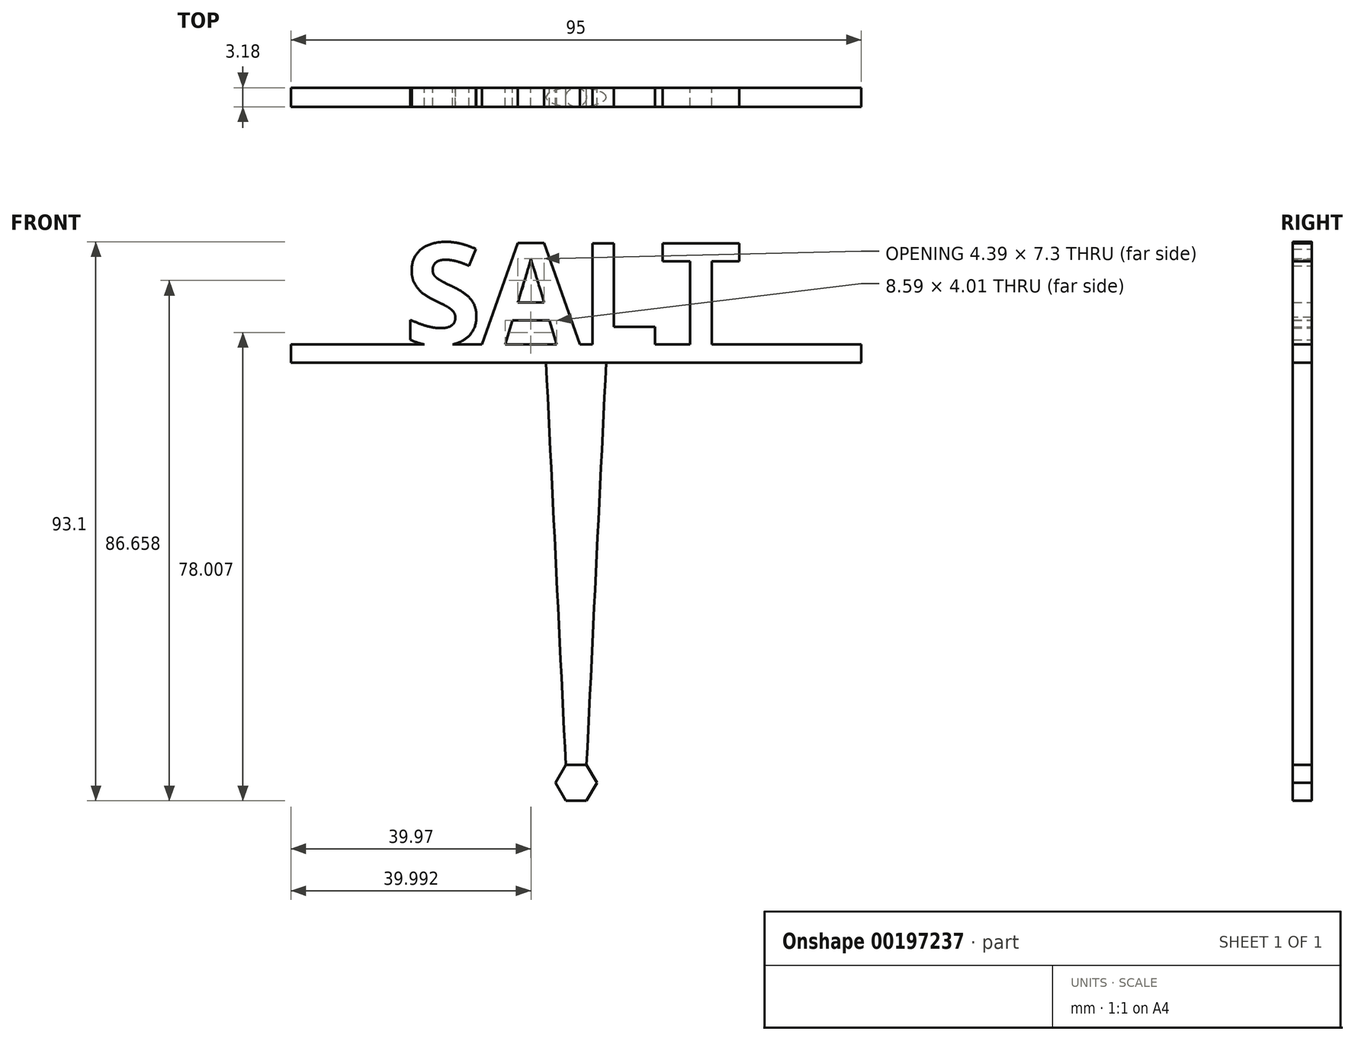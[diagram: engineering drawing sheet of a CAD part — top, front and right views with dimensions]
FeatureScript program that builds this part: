
annotation { "Feature Type Name" : "Feature", "Feature Type Description" : "" }
export const myFeature = defineFeature(function(context is Context, id is Id, definition is map)
    precondition{}
    {
        {
            var Q0;
            Q0=qCreatedBy(makeId("Front.planeOp"),FACE);
            var sketch = newSketch(context, id + "F0", { "sketchPlane" : qUnion([Q0])});
            skLineSegment(sketch, "E0.bottom", {"start": v(-47.5, 3) * mm, "end": v(47.5, 3) * mm});
            skLineSegment(sketch, "E0.top", {"start": v(-47.5, 0) * mm, "end": v(47.5, 0) * mm});
            skLineSegment(sketch, "E0.left", {"start": v(-47.5, 3) * mm, "end": v(-47.5, 0) * mm});
            skLineSegment(sketch, "E0.right", {"start": v(47.5, 3) * mm, "end": v(47.5, 0) * mm});
            skText(sketch, "E1", { "text": "SALT", "fontName": "OpenSans-Bold.ttf"});
            const initialGuessF0  = {"E1": [-0.02868, 0.003, 1, 0, 0.017]};
            skSetInitialGuess(sketch, initialGuessF0);
            skSolve(sketch);
        }
        {
            var Q0;
            Q0=qSketchRegion(id+"F0",true);
            extrude(context, id + "F1", {"entities" : qUnion([Q0]), "depth" : 3.17 * mm});
        }
        {
            var Q0;
            Q0=qCreatedBy(makeId("Top.planeOp"),FACE);
            var sketch = newSketch(context, id + "F2", { "sketchPlane" : qUnion([Q0])});
            skLineSegment(sketch, "E2.bottom", {"start": v(0, 0) * mm, "end": v(2.5, 0) * mm, "construction": true});
            skLineSegment(sketch, "E2.top", {"start": v(0, -3.17) * mm, "end": v(2.5, -3.17) * mm, "construction": true});
            skLineSegment(sketch, "E2.left", {"start": v(0, 0) * mm, "end": v(0, -3.18) * mm, "construction": true});
            skLineSegment(sketch, "E2.right", {"start": v(2.5, 0) * mm, "end": v(2.5, -3.17) * mm, "construction": true});
            skEllipse(sketch, "E3", {"center": v(0, -1.59) * mm, "majorRadius": 5 * mm, "minorRadius": 1.59 * mm, "majorAxis": v(1, 0)});
            skSolve(sketch);
        }
        {
            var Q0;
            Q0=qCreatedBy(makeId("Top.planeOp"),FACE);
            cPlane(context, id + "F3", {"entities" : qUnion([Q0]), "cplaneType" : CPlaneType.OFFSET, "offset" : 70 * mm, "oppositeDirection" : true, "width" : 150 * mm, "height" : 150 * mm});
        }
        {
            var Q0;
            Q0=qCreatedBy(id+"F3.planeOp",FACE);
            var sketch = newSketch(context, id + "F4", { "sketchPlane" : qUnion([Q0])});
            skPoint(sketch, "E4", {"position": v(0, 0) * mm});
            skLineSegment(sketch, "E5.0", {"start": v(-50.9, -1.59) * mm, "end": v(49.1, -1.59) * mm, "construction": true});
            skLineSegment(sketch, "E6.0", {"start": v(0, 0) * mm, "end": v(0, -3.17) * mm, "construction": true});
            skCircle(sketch, "E7", {"center": v(0, -1.59) * mm, "radius": 1.59 * mm});
            skSolve(sketch);
        }
        {
            var Q1;
            Q1=makeQuery(id+"F2.imprint","IMPRINT",FACE,{"disambiguationData":[TD([[makeQuery(id+"F2.imprint","IMPRINT",EDGE,{"derivedFrom":sQuery(id+"F2.wireOp",EDGE,"E3")}),1.0]])]});
            var Q2;
            Q2=makeQuery(id+"F4.imprint","IMPRINT",FACE,{"disambiguationData":[TD([[makeQuery(id+"F4.imprint","IMPRINT",EDGE,{"derivedFrom":sQuery(id+"F4.wireOp",EDGE,"E7")}),1.0]])]});
            loft(context, id + "F5", {"operationType" : NewBodyOperationType.ADD, "sheetProfilesArray" : [{ "sheetProfileEntities" : qUnion([Q1]) }, { "sheetProfileEntities" : qUnion([Q2]) }]});
        }
        {
            var Q0;
            Q0=qCreatedBy(makeId("Front.planeOp"),FACE);
            var sketch = newSketch(context, id + "F6", { "sketchPlane" : qUnion([Q0])});
            skLineSegment(sketch, "E8.bottom", {"start": v(3, -73) * mm, "end": v(-3, -73) * mm, "construction": true});
            skLineSegment(sketch, "E8.top", {"start": v(3, -67) * mm, "end": v(-3, -67) * mm, "construction": true});
            skLineSegment(sketch, "E8.left", {"start": v(3, -73) * mm, "end": v(3, -67) * mm, "construction": true});
            skLineSegment(sketch, "E8.right", {"start": v(-3, -73) * mm, "end": v(-3, -67) * mm, "construction": true});
            skPoint(sketch, "E8.middle", {"position": v(0, -70) * mm});
            skCircle(sketch, "E9.cCircle", {"center": v(0, -70) * mm, "radius": 3 * mm, "construction": true});
            skLineSegment(sketch, "E9.0", {"start": v(0, -73) * mm, "end": v(-2.6, -71.5) * mm, "construction": true});
            skLineSegment(sketch, "E9.1", {"start": v(-2.6, -71.5) * mm, "end": v(-2.6, -68.5) * mm, "construction": true});
            skLineSegment(sketch, "E9.2", {"start": v(-2.6, -68.5) * mm, "end": v(0, -67) * mm, "construction": true});
            skLineSegment(sketch, "E9.3", {"start": v(0, -67) * mm, "end": v(2.6, -68.5) * mm, "construction": true});
            skLineSegment(sketch, "E9.4", {"start": v(2.6, -68.5) * mm, "end": v(2.6, -71.5) * mm, "construction": true});
            skLineSegment(sketch, "E9.5", {"start": v(2.6, -71.5) * mm, "end": v(0, -73) * mm, "construction": true});
            skLineSegment(sketch, "E10.0", {"start": v(1.73, -73) * mm, "end": v(-1.73, -73) * mm});
            skLineSegment(sketch, "E10.1", {"start": v(-1.73, -73) * mm, "end": v(-3.46, -70) * mm});
            skLineSegment(sketch, "E10.2", {"start": v(-3.46, -70) * mm, "end": v(-1.73, -67) * mm});
            skLineSegment(sketch, "E10.3", {"start": v(-1.73, -67) * mm, "end": v(1.73, -67) * mm});
            skLineSegment(sketch, "E10.4", {"start": v(1.73, -67) * mm, "end": v(3.46, -70) * mm});
            skLineSegment(sketch, "E10.5", {"start": v(3.46, -70) * mm, "end": v(1.73, -73) * mm});
            skPoint(sketch, "E10.0.midPoint", {"position": v(0, -73) * mm});
            skSolve(sketch);
        }
        {
            var Q0;
            Q0=makeQuery(id+"F6.imprint","IMPRINT",FACE,{"disambiguationData":[TD([[makeQuery(id+"F6.imprint","IMPRINT",EDGE,{"derivedFrom":sQuery(id+"F6.wireOp",EDGE,"E10.0")}),-1.0]])]});
            extrude(context, id + "F7", {"entities" : qUnion([Q0]), "operationType" : NewBodyOperationType.ADD, "depth" : 3.17 * mm});
        }
    });
